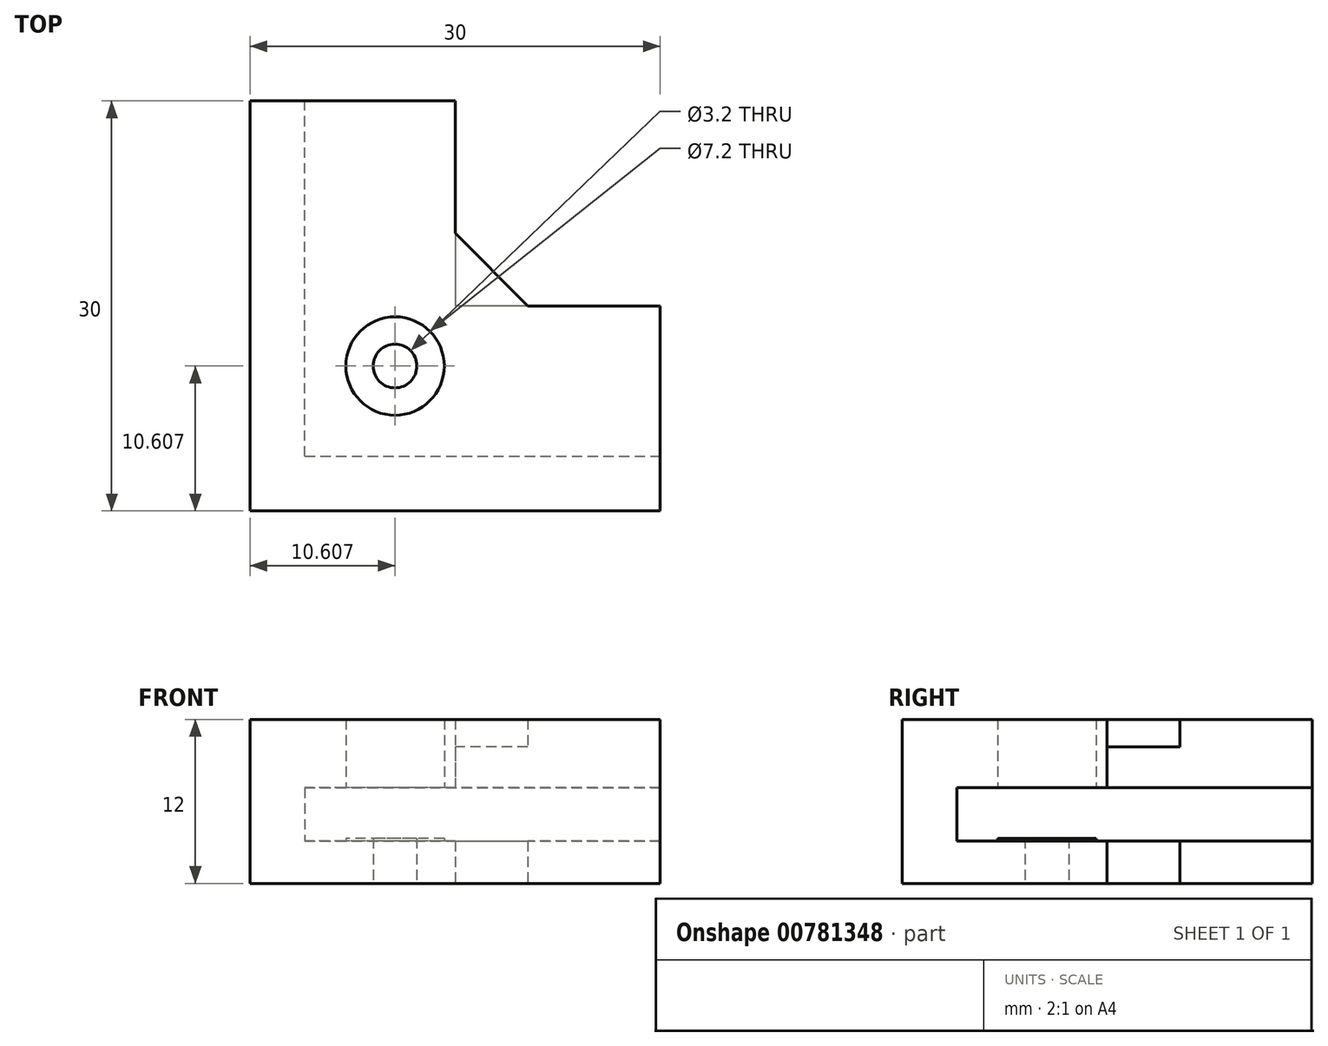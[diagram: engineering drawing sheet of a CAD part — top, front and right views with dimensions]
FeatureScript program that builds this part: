
annotation { "Feature Type Name" : "Feature", "Feature Type Description" : "" }
export const myFeature = defineFeature(function(context is Context, id is Id, definition is map)
    precondition{}
    {
        {
            var Q0;
            Q0=qCreatedBy(makeId("Top.planeOp"),FACE);
            var sketch = newSketch(context, id + "F0", { "sketchPlane" : qUnion([Q0])});
            skLineSegment(sketch, "E0.bottom", {"start": v(15, -15) * mm, "end": v(-15, -15) * mm});
            skLineSegment(sketch, "E0.top", {"start": v(0, 15) * mm, "end": v(-15, 15) * mm});
            skLineSegment(sketch, "E0.left", {"start": v(15, -15) * mm, "end": v(15, 0) * mm});
            skLineSegment(sketch, "E0.right", {"start": v(-15, -15) * mm, "end": v(-15, 15) * mm});
            skPoint(sketch, "E0.middle", {"position": v(0, 0) * mm});
            skLineSegment(sketch, "E1", {"start": v(0, 15) * mm, "end": v(0, -15) * mm, "construction": true});
            skLineSegment(sketch, "E2", {"start": v(-15, 0) * mm, "end": v(15, 0) * mm, "construction": true});
            skLineSegment(sketch, "E3.bottom", {"start": v(-15, 15) * mm, "end": v(0, 15) * mm});
            skLineSegment(sketch, "E3.top", {"start": v(-15, -15) * mm, "end": v(0, -15) * mm});
            skLineSegment(sketch, "E3.left", {"start": v(-15, 15) * mm, "end": v(-15, -15) * mm});
            skLineSegment(sketch, "E3.right", {"start": v(0, 15) * mm, "end": v(0, -15) * mm});
            skLineSegment(sketch, "E4.top", {"start": v(15, 0) * mm, "end": v(-15, 0) * mm});
            skLineSegment(sketch, "E4.right", {"start": v(-15, -15) * mm, "end": v(-15, 0) * mm});
            skArc(sketch, "E5", {"start": v(5.32, 0) * mm, "mid": v(3.76, 3.76) * mm, "end": v(0, 5.32) * mm, "construction": true});
            skLineSegment(sketch, "E6", {"start": v(0, 5.32) * mm, "end": v(5.32, 0) * mm});
            skLineSegment(sketch, "E7.bottom", {"start": v(-15, 15) * mm, "end": v(-7, 15) * mm});
            skLineSegment(sketch, "E7.top", {"start": v(-15, -15) * mm, "end": v(2.96, -15) * mm});
            skLineSegment(sketch, "E8.top", {"start": v(-15, -15) * mm, "end": v(15, -15) * mm});
            skLineSegment(sketch, "E8.left", {"start": v(-15, -7) * mm, "end": v(-15, -15) * mm});
            skLineSegment(sketch, "E8.right", {"start": v(15, -7) * mm, "end": v(15, -15) * mm});
            skPoint(sketch, "E9.orphan", {"position": v(15, 15) * mm});
            skLineSegment(sketch, "E10", {"start": v(-15, -11) * mm, "end": v(15, -11) * mm});
            skLineSegment(sketch, "E11", {"start": v(-11, -15) * mm, "end": v(-11, 15) * mm});
            skCircle(sketch, "E12", {"center": v(-15, -15) * mm, "radius": 15 * mm, "construction": true});
            skLineSegment(sketch, "E13", {"start": v(-15, -15) * mm, "end": v(0, 0) * mm, "construction": true});
            skCircle(sketch, "E14", {"center": v(-4.4, -4.4) * mm, "radius": 1.6 * mm});
            skCircle(sketch, "E15", {"center": v(-4.4, -4.4) * mm, "radius": 3.6 * mm});
            skSolve(sketch);
        }
        {
            var Q0;
            {var subQ1=sQuery(id+"F0.wireOp",EDGE,"E8.bottom");Q0=makeQuery(id+"F0.imprint","IMPRINT",FACE,{"disambiguationData":[TD([[makeQuery(id+"F0.imprint","IMPRINT",EDGE,{"derivedFrom":subQ1}),-1.0]])]});}
            var Q1;
            {var subQ0=sQuery(id+"F0.wireOp",EDGE,"E8.bottom");Q1=makeQuery(id+"F0.imprint","IMPRINT",FACE,{"disambiguationData":[TD([[makeQuery(id+"F0.imprint","IMPRINT",EDGE,{"derivedFrom":subQ0}),1.0]])]});}
            var Q2;
            {var subQ0=sQuery(id+"F0.wireOp",EDGE,"494a5b59-d94c-42f9-8c93-dc152082862d.trimOffspring");Q2=makeQuery(id+"F0.imprint","IMPRINT",FACE,{"disambiguationData":[TD([[makeQuery(id+"F0.imprint","IMPRINT",EDGE,{"derivedFrom":subQ0}),1.0]])]});}
            var Q3;
            {var subQ5=sQuery(id+"F0.wireOp",EDGE,"E7.bottom");Q3=makeQuery(id+"F0.imprint","IMPRINT",FACE,{"disambiguationData":[TD([[makeQuery(id+"F0.imprint","IMPRINT",EDGE,{"derivedFrom":subQ5}),-1.0]])]});}
            var Q4;
            {var subQ5=sQuery(id+"F0.wireOp",EDGE,"E8.right");Q4=makeQuery(id+"F0.imprint","IMPRINT",FACE,{"disambiguationData":[TD([[makeQuery(id+"F0.imprint","IMPRINT",EDGE,{"derivedFrom":subQ5}),-1.0]])]});}
            var Q5;
            {var subQ0=sQuery(id+"F0.wireOp",EDGE,"E0.left");Q5=makeQuery(id+"F0.imprint","IMPRINT",FACE,{"disambiguationData":[TD([[makeQuery(id+"F0.imprint","IMPRINT",EDGE,{"derivedFrom":subQ0}),1.0]])]});}
            var Q6;
            {var subQ3=sQuery(id+"F0.wireOp",EDGE,"E4.top");var subQ7=sQuery(id+"F0.wireOp",EDGE,"E3.right");var subQ8=makeQuery(id+"F0.imprint","INTERSECT",VERTEX,{"derivedFrom":[subQ7,subQ3]});Q6=makeQuery(id+"F0.imprint","IMPRINT",FACE,{"disambiguationData":[TD([[makeQuery(id+"F0.imprint","IMPRINT",EDGE,{"disambiguationData":[TD([[subQ8,-1.0]])],"derivedFrom":subQ7}),-1.0]])]});}
            var Q7;
            {var subQ6=sQuery(id+"F0.wireOp",EDGE,"E3.bottom");Q7=makeQuery(id+"F0.imprint","IMPRINT",FACE,{"disambiguationData":[TD([[makeQuery(id+"F0.imprint","IMPRINT",EDGE,{"derivedFrom":subQ6}),-1.0]])]});}
            var Q8;
            {var subQ0=sQuery(id+"F0.wireOp",EDGE,"E6");Q8=makeQuery(id+"F0.imprint","IMPRINT",FACE,{"disambiguationData":[TD([[makeQuery(id+"F0.imprint","IMPRINT",EDGE,{"derivedFrom":subQ0}),-1.0]])]});}
            var Q9;
            {var subQ0=sQuery(id+"F0.wireOp",EDGE,"E8.left");var subQ1=sQuery(id+"F0.wireOp",EDGE,"E8.top");var subQ2=makeQuery(id+"F0.imprint","INTERSECT",VERTEX,{"derivedFrom":[subQ1,subQ0]});Q9=makeQuery(id+"F0.imprint","IMPRINT",FACE,{"disambiguationData":[TD([[makeQuery(id+"F0.imprint","IMPRINT",EDGE,{"disambiguationData":[TD([[subQ2,-1.0]])],"derivedFrom":subQ1}),1.0]])]});}
            var Q10;
            {var subQ0=sQuery(id+"F0.wireOp",EDGE,"494a5b59-d94c-42f9-8c93-dc152082862d.trimOffspring");var subQ1=sQuery(id+"F0.wireOp",EDGE,"E8.top");var subQ2=makeQuery(id+"F0.imprint","INTERSECT",VERTEX,{"derivedFrom":[subQ1,subQ0]});Q10=makeQuery(id+"F0.imprint","IMPRINT",FACE,{"disambiguationData":[TD([[makeQuery(id+"F0.imprint","IMPRINT",EDGE,{"disambiguationData":[TD([[subQ2,1.0]])],"derivedFrom":subQ1}),1.0]])]});}
            var Q11;
            {var subQ1=sQuery(id+"F0.wireOp",EDGE,"d452e2ad-344b-4883-a8ab-68da911cf365.trimOffspring");var subQ5=sQuery(id+"F0.wireOp",EDGE,"E3.right");var subQ6=makeQuery(id+"F0.imprint","INTERSECT",VERTEX,{"derivedFrom":[subQ5,subQ1]});Q11=makeQuery(id+"F0.imprint","IMPRINT",FACE,{"disambiguationData":[TD([[makeQuery(id+"F0.imprint","IMPRINT",EDGE,{"disambiguationData":[TD([[subQ6,-1.0]])],"derivedFrom":subQ5}),-1.0]])]});}
            var Q12;
            {var subQ3=sQuery(id+"F0.wireOp",EDGE,"54lul5Wj-MHDL-55nK-tijT-qi4xbZ7w2Bcx");var subQ7=sQuery(id+"F0.wireOp",EDGE,"E8.bottom");var subQ8=makeQuery(id+"F0.imprint","INTERSECT",VERTEX,{"derivedFrom":[subQ7,subQ3]});Q12=makeQuery(id+"F0.imprint","IMPRINT",FACE,{"disambiguationData":[TD([[makeQuery(id+"F0.imprint","IMPRINT",EDGE,{"disambiguationData":[TD([[subQ8,1.0]])],"derivedFrom":subQ7}),-1.0]])]});}
            var Q13;
            {var subQ7=sQuery(id+"F0.wireOp",EDGE,"E7.right");var subQ8=sQuery(id+"F0.wireOp",EDGE,"E4.top");var subQ9=makeQuery(id+"F0.imprint","INTERSECT",VERTEX,{"derivedFrom":[subQ8,subQ7]});Q13=makeQuery(id+"F0.imprint","IMPRINT",FACE,{"disambiguationData":[TD([[makeQuery(id+"F0.imprint","IMPRINT",EDGE,{"disambiguationData":[TD([[subQ9,-1.0]])],"derivedFrom":subQ8}),1.0]])]});}
            var Q14;
            {var subQ3=sQuery(id+"F0.wireOp",EDGE,"54lul5Wj-MHDL-55nK-tijT-qi4xbZ7w2Bcx");var subQ5=sQuery(id+"F0.wireOp",EDGE,"d452e2ad-344b-4883-a8ab-68da911cf365.trimOffspring");var subQ6=makeQuery(id+"F0.imprint","INTERSECT",VERTEX,{"derivedFrom":[subQ5,subQ3]});Q14=makeQuery(id+"F0.imprint","IMPRINT",FACE,{"disambiguationData":[TD([[makeQuery(id+"F0.imprint","IMPRINT",EDGE,{"disambiguationData":[TD([[subQ6,-1.0]])],"derivedFrom":subQ5}),1.0]])]});}
            var Q15;
            {var subQ0=sQuery(id+"F0.wireOp",EDGE,"54lul5Wj-MHDL-55nK-tijT-qi4xbZ7w2Bcx");var subQ1=sQuery(id+"F0.wireOp",EDGE,"E8.bottom");var subQ2=makeQuery(id+"F0.imprint","INTERSECT",VERTEX,{"derivedFrom":[subQ1,subQ0]});Q15=makeQuery(id+"F0.imprint","IMPRINT",FACE,{"disambiguationData":[TD([[makeQuery(id+"F0.imprint","IMPRINT",EDGE,{"disambiguationData":[TD([[subQ2,1.0]])],"derivedFrom":subQ1}),1.0]])]});}
            var Q16;
            {var subQ0=sQuery(id+"F0.wireOp",EDGE,"54lul5Wj-MHDL-55nK-tijT-qi4xbZ7w2Bcx");var subQ1=sQuery(id+"F0.wireOp",EDGE,"d452e2ad-344b-4883-a8ab-68da911cf365.trimOffspring");var subQ2=makeQuery(id+"F0.imprint","INTERSECT",VERTEX,{"derivedFrom":[subQ1,subQ0]});Q16=makeQuery(id+"F0.imprint","IMPRINT",FACE,{"disambiguationData":[TD([[makeQuery(id+"F0.imprint","IMPRINT",EDGE,{"disambiguationData":[TD([[subQ2,-1.0]])],"derivedFrom":subQ1}),-1.0]])]});}
            var Q17;
            {var subQ3=sQuery(id+"F0.wireOp",EDGE,"E11");var subQ5=sQuery(id+"F0.wireOp",EDGE,"E8.bottom");var subQ6=makeQuery(id+"F0.imprint","INTERSECT",VERTEX,{"derivedFrom":[subQ5,subQ3]});Q17=makeQuery(id+"F0.imprint","IMPRINT",FACE,{"disambiguationData":[TD([[makeQuery(id+"F0.imprint","IMPRINT",EDGE,{"disambiguationData":[TD([[subQ6,-1.0]])],"derivedFrom":subQ5}),-1.0]])]});}
            var Q18;
            {var subQ5=sQuery(id+"F0.wireOp",EDGE,"E3.left");var subQ6=sQuery(id+"F0.wireOp",EDGE,"E4.top");var subQ7=makeQuery(id+"F0.imprint","INTERSECT",VERTEX,{"derivedFrom":[subQ6,subQ5]});Q18=makeQuery(id+"F0.imprint","IMPRINT",FACE,{"disambiguationData":[TD([[makeQuery(id+"F0.imprint","IMPRINT",EDGE,{"disambiguationData":[TD([[subQ7,1.0]])],"derivedFrom":subQ6}),1.0]])]});}
            var Q19;
            {var subQ1=sQuery(id+"F0.wireOp",EDGE,"E3.right");var subQ5=sQuery(id+"F0.wireOp",EDGE,"E8.top");var subQ6=makeQuery(id+"F0.imprint","INTERSECT",VERTEX,{"derivedFrom":[subQ1,subQ5]});Q19=makeQuery(id+"F0.imprint","IMPRINT",FACE,{"disambiguationData":[TD([[makeQuery(id+"F0.imprint","IMPRINT",EDGE,{"disambiguationData":[TD([[subQ6,1.0]])],"derivedFrom":subQ1}),-1.0]])]});}
            var Q20;
            {var subQ0=sQuery(id+"F0.wireOp",EDGE,"E14");var subQ1=sQuery(id+"F0.wireOp",EDGE,"E10");var subQ2=makeQuery(id+"F0.imprint","INTERSECT",VERTEX,{"disambiguationData":[OD(1.0)],"derivedFrom":[subQ1,subQ0]});Q20=makeQuery(id+"F0.imprint","IMPRINT",FACE,{"disambiguationData":[TD([[makeQuery(id+"F0.imprint","IMPRINT",EDGE,{"disambiguationData":[TD([[subQ2,-1.0]])],"derivedFrom":subQ1}),1.0]])]});}
            var Q21;
            {var subQ0=sQuery(id+"F0.wireOp",EDGE,"E14");var subQ1=sQuery(id+"F0.wireOp",EDGE,"E10");var subQ2=makeQuery(id+"F0.imprint","INTERSECT",VERTEX,{"disambiguationData":[OD(1.0)],"derivedFrom":[subQ1,subQ0]});Q21=makeQuery(id+"F0.imprint","IMPRINT",FACE,{"disambiguationData":[TD([[makeQuery(id+"F0.imprint","IMPRINT",EDGE,{"disambiguationData":[TD([[subQ2,-1.0]])],"derivedFrom":subQ1}),-1.0]])]});}
            var Q22;
            {var subQ0=sQuery(id+"F0.wireOp",EDGE,"E11");var subQ1=sQuery(id+"F0.wireOp",EDGE,"E10");var subQ2=makeQuery(id+"F0.imprint","INTERSECT",VERTEX,{"derivedFrom":[subQ1,subQ0]});Q22=makeQuery(id+"F0.imprint","IMPRINT",FACE,{"disambiguationData":[TD([[makeQuery(id+"F0.imprint","IMPRINT",EDGE,{"disambiguationData":[TD([[subQ2,-1.0]])],"derivedFrom":subQ1}),1.0]])]});}
            var Q23;
            {var subQ0=sQuery(id+"F0.wireOp",EDGE,"E15");var subQ1=sQuery(id+"F0.wireOp",EDGE,"E11");var subQ2=makeQuery(id+"F0.imprint","INTERSECT",VERTEX,{"disambiguationData":[OD(0.0)],"derivedFrom":[subQ1,subQ0]});Q23=makeQuery(id+"F0.imprint","IMPRINT",FACE,{"disambiguationData":[TD([[makeQuery(id+"F0.imprint","IMPRINT",EDGE,{"disambiguationData":[TD([[subQ2,-1.0]])],"derivedFrom":subQ1}),1.0]])]});}
            var Q24;
            {var subQ0=sQuery(id+"F0.wireOp",EDGE,"E15");var subQ1=sQuery(id+"F0.wireOp",EDGE,"E10");var subQ2=makeQuery(id+"F0.imprint","INTERSECT",VERTEX,{"disambiguationData":[OD(0.0)],"derivedFrom":[subQ1,subQ0]});Q24=makeQuery(id+"F0.imprint","IMPRINT",FACE,{"disambiguationData":[TD([[makeQuery(id+"F0.imprint","IMPRINT",EDGE,{"disambiguationData":[TD([[subQ2,-1.0]])],"derivedFrom":subQ1}),-1.0]])]});}
            var Q25;
            Q25=makeQuery(id+"F0.imprint","IMPRINT",FACE,{"disambiguationData":[TD([[makeQuery(id+"F0.imprint","IMPRINT",EDGE,{"derivedFrom":sQuery(id+"F0.wireOp",EDGE,"E14")}),-1.0]])]});
            extrude(context, id + "F1", {"entities" : qUnion([Q0, Q1, Q2, Q3, Q4, Q5, Q6, Q7, Q8, Q9, Q10, Q11, Q12, Q13, Q14, Q15, Q16, Q17, Q18, Q19, Q20, Q21, Q22, Q23, Q24, Q25]), "depth" : 12 * mm, "offsetDistance" : 25 * mm});
        }
        {
            var Q0;
            {var subQ0=sQuery(id+"F0.wireOp",EDGE,"E0.left");Q0=makeQuery(id+"F0.imprint","IMPRINT",FACE,{"disambiguationData":[TD([[makeQuery(id+"F0.imprint","IMPRINT",EDGE,{"derivedFrom":subQ0}),1.0]])]});}
            var Q1;
            {var subQ3=sQuery(id+"F0.wireOp",EDGE,"E4.top");var subQ7=sQuery(id+"F0.wireOp",EDGE,"E3.right");var subQ8=makeQuery(id+"F0.imprint","INTERSECT",VERTEX,{"derivedFrom":[subQ7,subQ3]});Q1=makeQuery(id+"F0.imprint","IMPRINT",FACE,{"disambiguationData":[TD([[makeQuery(id+"F0.imprint","IMPRINT",EDGE,{"disambiguationData":[TD([[subQ8,-1.0]])],"derivedFrom":subQ7}),-1.0]])]});}
            var Q2;
            {var subQ6=sQuery(id+"F0.wireOp",EDGE,"E3.bottom");Q2=makeQuery(id+"F0.imprint","IMPRINT",FACE,{"disambiguationData":[TD([[makeQuery(id+"F0.imprint","IMPRINT",EDGE,{"derivedFrom":subQ6}),-1.0]])]});}
            var Q3;
            {var subQ0=sQuery(id+"F0.wireOp",EDGE,"E6");Q3=makeQuery(id+"F0.imprint","IMPRINT",FACE,{"disambiguationData":[TD([[makeQuery(id+"F0.imprint","IMPRINT",EDGE,{"derivedFrom":subQ0}),-1.0]])]});}
            var Q4;
            {var subQ1=sQuery(id+"F0.wireOp",EDGE,"d452e2ad-344b-4883-a8ab-68da911cf365.trimOffspring");var subQ5=sQuery(id+"F0.wireOp",EDGE,"E3.right");var subQ6=makeQuery(id+"F0.imprint","INTERSECT",VERTEX,{"derivedFrom":[subQ5,subQ1]});Q4=makeQuery(id+"F0.imprint","IMPRINT",FACE,{"disambiguationData":[TD([[makeQuery(id+"F0.imprint","IMPRINT",EDGE,{"disambiguationData":[TD([[subQ6,-1.0]])],"derivedFrom":subQ5}),-1.0]])]});}
            var Q5;
            {var subQ7=sQuery(id+"F0.wireOp",EDGE,"E7.right");var subQ8=sQuery(id+"F0.wireOp",EDGE,"E4.top");var subQ9=makeQuery(id+"F0.imprint","INTERSECT",VERTEX,{"derivedFrom":[subQ8,subQ7]});Q5=makeQuery(id+"F0.imprint","IMPRINT",FACE,{"disambiguationData":[TD([[makeQuery(id+"F0.imprint","IMPRINT",EDGE,{"disambiguationData":[TD([[subQ9,-1.0]])],"derivedFrom":subQ8}),1.0]])]});}
            var Q6;
            {var subQ0=sQuery(id+"F0.wireOp",EDGE,"d452e2ad-344b-4883-a8ab-68da911cf365.trimOffspring");var subQ1=sQuery(id+"F0.wireOp",EDGE,"E3.right");var subQ2=makeQuery(id+"F0.imprint","INTERSECT",VERTEX,{"derivedFrom":[subQ1,subQ0]});Q6=makeQuery(id+"F0.imprint","IMPRINT",FACE,{"disambiguationData":[TD([[makeQuery(id+"F0.imprint","IMPRINT",EDGE,{"disambiguationData":[TD([[subQ2,-1.0]])],"derivedFrom":subQ1}),1.0]])]});}
            var Q7;
            {var subQ0=sQuery(id+"F0.wireOp",EDGE,"E7.right");var subQ1=sQuery(id+"F0.wireOp",EDGE,"E4.top");var subQ2=makeQuery(id+"F0.imprint","INTERSECT",VERTEX,{"derivedFrom":[subQ1,subQ0]});Q7=makeQuery(id+"F0.imprint","IMPRINT",FACE,{"disambiguationData":[TD([[makeQuery(id+"F0.imprint","IMPRINT",EDGE,{"disambiguationData":[TD([[subQ2,-1.0]])],"derivedFrom":subQ1}),-1.0]])]});}
            var Q8;
            {var subQ3=sQuery(id+"F0.wireOp",EDGE,"E11");var subQ5=sQuery(id+"F0.wireOp",EDGE,"E8.bottom");var subQ6=makeQuery(id+"F0.imprint","INTERSECT",VERTEX,{"derivedFrom":[subQ5,subQ3]});Q8=makeQuery(id+"F0.imprint","IMPRINT",FACE,{"disambiguationData":[TD([[makeQuery(id+"F0.imprint","IMPRINT",EDGE,{"disambiguationData":[TD([[subQ6,-1.0]])],"derivedFrom":subQ5}),-1.0]])]});}
            var Q9;
            {var subQ0=sQuery(id+"F0.wireOp",EDGE,"54lul5Wj-MHDL-55nK-tijT-qi4xbZ7w2Bcx");var subQ1=sQuery(id+"F0.wireOp",EDGE,"E8.bottom");var subQ2=makeQuery(id+"F0.imprint","INTERSECT",VERTEX,{"derivedFrom":[subQ1,subQ0]});Q9=makeQuery(id+"F0.imprint","IMPRINT",FACE,{"disambiguationData":[TD([[makeQuery(id+"F0.imprint","IMPRINT",EDGE,{"disambiguationData":[TD([[subQ2,1.0]])],"derivedFrom":subQ1}),1.0]])]});}
            var Q10;
            {var subQ3=sQuery(id+"F0.wireOp",EDGE,"54lul5Wj-MHDL-55nK-tijT-qi4xbZ7w2Bcx");var subQ5=sQuery(id+"F0.wireOp",EDGE,"d452e2ad-344b-4883-a8ab-68da911cf365.trimOffspring");var subQ6=makeQuery(id+"F0.imprint","INTERSECT",VERTEX,{"derivedFrom":[subQ5,subQ3]});Q10=makeQuery(id+"F0.imprint","IMPRINT",FACE,{"disambiguationData":[TD([[makeQuery(id+"F0.imprint","IMPRINT",EDGE,{"disambiguationData":[TD([[subQ6,-1.0]])],"derivedFrom":subQ5}),1.0]])]});}
            var Q11;
            {var subQ0=sQuery(id+"F0.wireOp",EDGE,"54lul5Wj-MHDL-55nK-tijT-qi4xbZ7w2Bcx");var subQ1=sQuery(id+"F0.wireOp",EDGE,"d452e2ad-344b-4883-a8ab-68da911cf365.trimOffspring");var subQ2=makeQuery(id+"F0.imprint","INTERSECT",VERTEX,{"derivedFrom":[subQ1,subQ0]});Q11=makeQuery(id+"F0.imprint","IMPRINT",FACE,{"disambiguationData":[TD([[makeQuery(id+"F0.imprint","IMPRINT",EDGE,{"disambiguationData":[TD([[subQ2,-1.0]])],"derivedFrom":subQ1}),-1.0]])]});}
            var Q12;
            {var subQ3=sQuery(id+"F0.wireOp",EDGE,"54lul5Wj-MHDL-55nK-tijT-qi4xbZ7w2Bcx");var subQ5=sQuery(id+"F0.wireOp",EDGE,"E8.bottom");var subQ6=makeQuery(id+"F0.imprint","INTERSECT",VERTEX,{"derivedFrom":[subQ5,subQ3]});Q12=makeQuery(id+"F0.imprint","IMPRINT",FACE,{"disambiguationData":[TD([[makeQuery(id+"F0.imprint","IMPRINT",EDGE,{"disambiguationData":[TD([[subQ6,1.0]])],"derivedFrom":subQ5}),-1.0]])]});}
            extrude(context, id + "F2", {"entities" : qUnion([Q0, Q1, Q2, Q3, Q4, Q5, Q6, Q7, Q8, Q9, Q10, Q11, Q12]), "operationType" : NewBodyOperationType.REMOVE, "depth" : 7 * mm, "offsetDistance" : 25 * mm, "hasSecondDirection" : true, "secondDirectionOppositeDirection" : false, "secondDirectionDepth" : 3.1 * mm});
        }
        {
            var Q0;
            {var subQ0=sQuery(id+"F0.wireOp",EDGE,"E6");Q0=makeQuery(id+"F0.imprint","IMPRINT",FACE,{"disambiguationData":[TD([[makeQuery(id+"F0.imprint","IMPRINT",EDGE,{"derivedFrom":subQ0}),-1.0]])]});}
            extrude(context, id + "F3", {"entities" : qUnion([Q0]), "operationType" : NewBodyOperationType.REMOVE, "depth" : 10 * mm, "offsetDistance" : 25 * mm, "hasSecondDirection" : true, "secondDirectionOppositeDirection" : false, "secondDirectionDepth" : 5 * mm});
        }
        {
            var Q0;
            Q0=makeQuery(id+"F0.imprint","IMPRINT",FACE,{"disambiguationData":[TD([[makeQuery(id+"F0.imprint","IMPRINT",EDGE,{"derivedFrom":sQuery(id+"F0.wireOp",EDGE,"E14")}),-1.0]])]});
            extrude(context, id + "F4", {"entities" : qUnion([Q0]), "operationType" : NewBodyOperationType.REMOVE, "depth" : 22.5 * mm, "offsetDistance" : 25 * mm, "hasSecondDirection" : true, "secondDirectionOppositeDirection" : false, "secondDirectionDepth" : 3.3 * mm});
        }
    });
